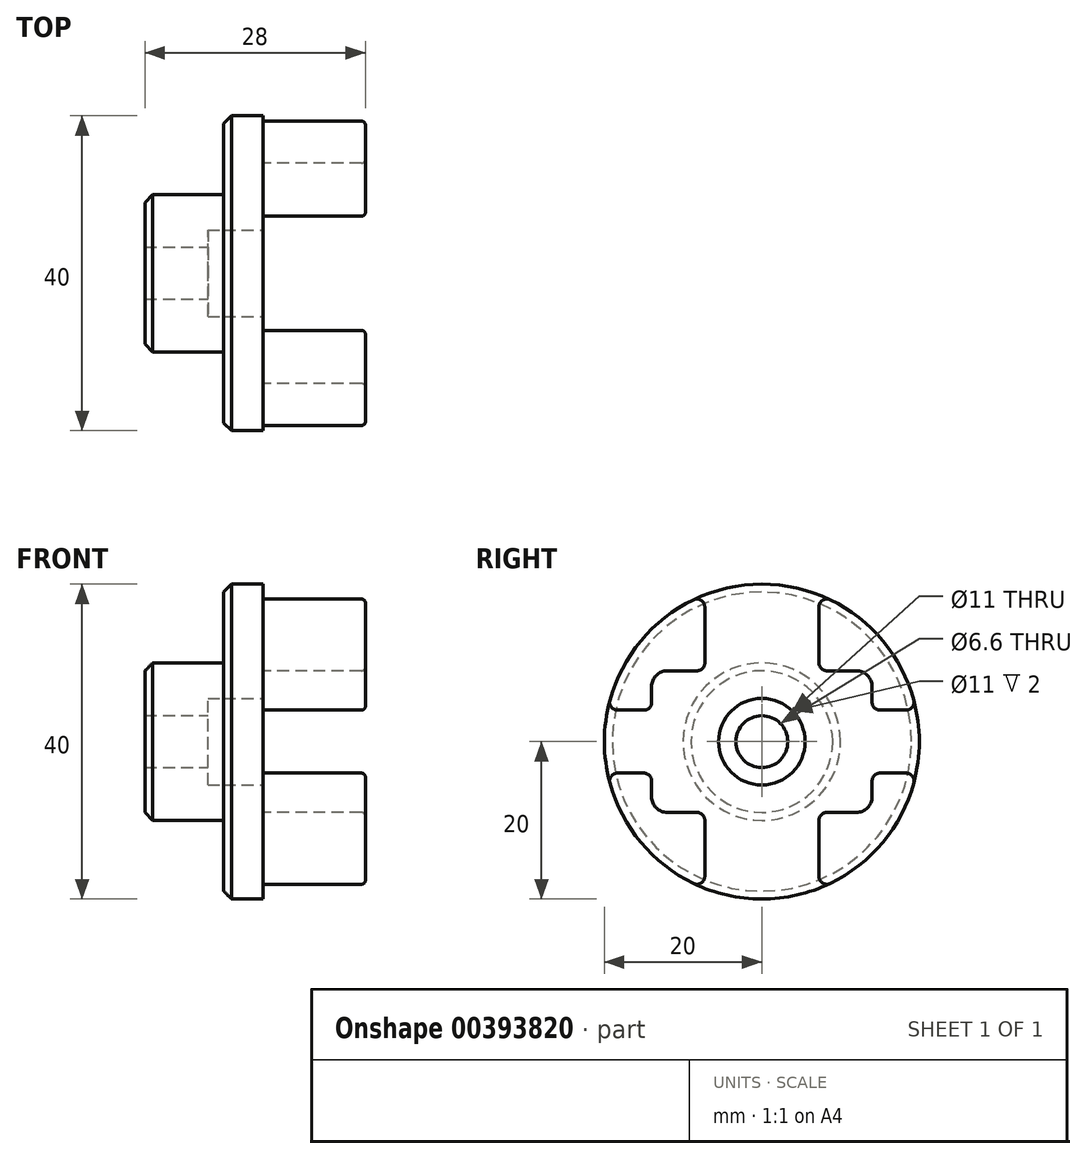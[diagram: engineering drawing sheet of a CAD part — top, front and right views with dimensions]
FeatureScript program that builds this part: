
annotation { "Feature Type Name" : "Feature", "Feature Type Description" : "" }
export const myFeature = defineFeature(function(context is Context, id is Id, definition is map)
    precondition{}
    {
        {
            var Q0;
            Q0=qCreatedBy(makeId("Front.planeOp"),FACE);
            var sketch = newSketch(context, id + "F0", { "sketchPlane" : qUnion([Q0])});
            skLineSegment(sketch, "E0", {"start": v(0, 0) * mm, "end": v(51.78, 0) * mm, "construction": true});
            skLineSegment(sketch, "E1", {"start": v(0, 10) * mm, "end": v(10, 10) * mm});
            skLineSegment(sketch, "E2", {"start": v(10, 10) * mm, "end": v(10, 0) * mm});
            skLineSegment(sketch, "E3", {"start": v(10, 0) * mm, "end": v(0, 0) * mm});
            skLineSegment(sketch, "E4", {"start": v(0, 0) * mm, "end": v(0, 10) * mm});
            skSolve(sketch);
        }
        {
            var Q0;
            Q0=qSketchRegion(id+"F0",true);
            var Q1;
            Q1=sQuery(id+"F0.wireOp",EDGE,"E0");
            revolve(context, id + "F1", {"entities" : qUnion([Q0]), "axis" : qUnion([Q1]), "revolveType" : RevolveType.FULL});
        }
        {
            var Q0;
            Q0=makeQuery(id+"F1.opRevolve","SWEPT_FACE",FACE,{"disambiguationData":[OSD([sQuery(id+"F0.wireOp",EDGE,"E2")])]});
            var sketch = newSketch(context, id + "F2", { "sketchPlane" : qUnion([Q0])});
            skLineSegment(sketch, "E5", {"start": v(-8.25, 5.65) * mm, "end": v(-8.25, -5.65) * mm});
            skLineSegment(sketch, "E6", {"start": v(0, 0) * mm, "end": v(0, 17.13) * mm, "construction": true});
            skLineSegment(sketch, "E7.MirrorCS", {"start": v(8.25, 5.65) * mm, "end": v(8.25, -5.65) * mm});
            skArc(sketch, "E8.0", {"start": v(-8.25, 5.65) * mm, "mid": v(-10, 0) * mm, "end": v(-8.25, -5.65) * mm});
            skArc(sketch, "E9.trimOffspring", {"start": v(8.25, -5.65) * mm, "mid": v(10, 0) * mm, "end": v(8.25, 5.65) * mm});
            skSolve(sketch);
        }
        {
            var Q0;
            Q0=qCreatedBy(makeId("Top.planeOp"),FACE);
            var sketch = newSketch(context, id + "F3", { "sketchPlane" : qUnion([Q0])});
            skCircle(sketch, "E10.cCircle", {"center": v(26, 0) * mm, "radius": 12.7 * mm, "construction": true});
            skLineSegment(sketch, "E10.0", {"start": v(26, 12.7) * mm, "end": v(37, 6.35) * mm});
            skLineSegment(sketch, "E10.1", {"start": v(37, 6.35) * mm, "end": v(37, -6.35) * mm});
            skLineSegment(sketch, "E10.2", {"start": v(37, -6.35) * mm, "end": v(26, -12.7) * mm});
            skLineSegment(sketch, "E10.3", {"start": v(26, -12.7) * mm, "end": v(15, -6.35) * mm});
            skLineSegment(sketch, "E10.4", {"start": v(15, -6.35) * mm, "end": v(15, 6.35) * mm});
            skLineSegment(sketch, "E10.5", {"start": v(15, 6.35) * mm, "end": v(26, 12.7) * mm});
            skLineSegment(sketch, "E11", {"start": v(0, 0) * mm, "end": v(49.29, 0) * mm, "construction": true});
            skLineSegment(sketch, "E12.0", {"start": v(10, -10) * mm, "end": v(10, 10) * mm, "construction": true});
            skLineSegment(sketch, "E13", {"start": v(20, -10) * mm, "end": v(0, -10) * mm});
            skSolve(sketch);
        }
        {
            var Q0;
            Q0=makeQuery(id+"F1.opRevolve","SWEPT_FACE",FACE,{"disambiguationData":[OSD([sQuery(id+"F0.wireOp",EDGE,"E2")])]});
            var sketch = newSketch(context, id + "F4", { "sketchPlane" : qUnion([Q0])});
            skCircle(sketch, "E14", {"center": v(0, 0) * mm, "radius": 20 * mm});
            skSolve(sketch);
        }
        {
            var Q0;
            Q0=qSketchRegion(id+"F4",true);
            extrude(context, id + "F5", {"entities" : qUnion([Q0]), "depth" : 5 * mm});
        }
        {
            var Q0;
            Q0=makeQuery(id+"F5.opExtrude","CAP_FACE",FACE,{"disambiguationData":[OSD([sQuery(id+"F4.wireOp",EDGE,"E14")])],"isStart":false});
            var sketch = newSketch(context, id + "F6", { "sketchPlane" : qUnion([Q0])});
            skLineSegment(sketch, "E15", {"start": v(0, -17) * mm, "end": v(0, 21.67) * mm, "construction": true});
            skLineSegment(sketch, "E16", {"start": v(-7.25, -10) * mm, "end": v(-7.25, -17.12) * mm});
            skLineSegment(sketch, "E17", {"start": v(-14, -7) * mm, "end": v(-14, -5) * mm});
            skArc(sketch, "E18.0", {"start": v(-19.3, -5.26) * mm, "mid": v(-15.37, -12.8) * mm, "end": v(-8.68, -18.02) * mm});
            skArc(sketch, "E19.trimOffspring", {"start": v(9.57, -17.56) * mm, "mid": v(19.9, -1.96) * mm, "end": v(12.8, 15.37) * mm});
            skPoint(sketch, "E20.visualSharp", {"position": v(-7.25, -18.64) * mm});
            skArc(sketch, "E20.filletArc", {"start": v(-8.68, -18.02) * mm, "mid": v(-7.72, -17.96) * mm, "end": v(-7.25, -17.12) * mm});
            skLineSegment(sketch, "E21", {"start": v(-18.33, -4) * mm, "end": v(-15, -4) * mm});
            skLineSegment(sketch, "E22", {"start": v(0, 0) * mm, "end": v(-17.48, 0) * mm, "construction": true});
            skPoint(sketch, "E23.newPointB", {"position": v(-12.8, 15.37) * mm});
            skArc(sketch, "E23.filletArc", {"start": v(-18.33, -4) * mm, "mid": v(-19.13, -4.4) * mm, "end": v(-19.3, -5.26) * mm});
            skPoint(sketch, "E24.visualSharp", {"position": v(-14, -4) * mm});
            skArc(sketch, "E24.filletArc", {"start": v(-14, -5) * mm, "mid": v(-14.3, -4.3) * mm, "end": v(-15, -4) * mm});
            skLineSegment(sketch, "E25", {"start": v(-12, -9) * mm, "end": v(-8.25, -9) * mm});
            skPoint(sketch, "E26.visualSharp", {"position": v(-14, -9) * mm});
            skArc(sketch, "E26.filletArc", {"start": v(-14, -7) * mm, "mid": v(-13.41, -8.41) * mm, "end": v(-12, -9) * mm});
            skPoint(sketch, "E27.visualSharp", {"position": v(-7.25, -9) * mm});
            skArc(sketch, "E27.filletArc", {"start": v(-7.25, -10) * mm, "mid": v(-7.54, -9.3) * mm, "end": v(-8.25, -9) * mm});
            skPoint(sketch, "E28.MirrorP", {"position": v(7.25, -18.64) * mm});
            skArc(sketch, "E29.MirrorCS", {"start": v(14, -5) * mm, "mid": v(14.3, -4.3) * mm, "end": v(15, -4) * mm});
            skArc(sketch, "E30.MirrorCS", {"start": v(8.68, -18.02) * mm, "mid": v(7.72, -17.96) * mm, "end": v(7.25, -17.12) * mm});
            skPoint(sketch, "E31.MirrorP", {"position": v(14, -4) * mm});
            skPoint(sketch, "E32.MirrorP", {"position": v(14, -9) * mm});
            skLineSegment(sketch, "E33.MirrorCS", {"start": v(18.33, -4) * mm, "end": v(15, -4) * mm});
            skArc(sketch, "E34.MirrorCS", {"start": v(7.25, -10) * mm, "mid": v(7.54, -9.3) * mm, "end": v(8.25, -9) * mm});
            skPoint(sketch, "E35.MirrorP", {"position": v(7.25, -9) * mm});
            skArc(sketch, "E36.MirrorCS", {"start": v(14, -7) * mm, "mid": v(13.41, -8.41) * mm, "end": v(12, -9) * mm});
            skLineSegment(sketch, "E37.MirrorCS", {"start": v(12, -9) * mm, "end": v(8.25, -9) * mm});
            skArc(sketch, "E38.MirrorCS", {"start": v(18.33, -4) * mm, "mid": v(19.13, -4.4) * mm, "end": v(19.3, -5.26) * mm});
            skArc(sketch, "E39.MirrorCS", {"start": v(19.3, -5.26) * mm, "mid": v(15.37, -12.8) * mm, "end": v(8.68, -18.02) * mm});
            skLineSegment(sketch, "E40.MirrorCS", {"start": v(14, -7) * mm, "end": v(14, -5) * mm});
            skLineSegment(sketch, "E41.MirrorCS", {"start": v(7.25, -10) * mm, "end": v(7.25, -17.12) * mm});
            skPoint(sketch, "E42.MirrorP", {"position": v(14, 9) * mm});
            skArc(sketch, "E43.MirrorCS", {"start": v(19.3, 5.26) * mm, "mid": v(15.37, 12.8) * mm, "end": v(8.68, 18.02) * mm});
            skPoint(sketch, "E44.MirrorP", {"position": v(-7.25, 18.64) * mm});
            skArc(sketch, "E45.MirrorCS", {"start": v(14, 7) * mm, "mid": v(13.41, 8.41) * mm, "end": v(12, 9) * mm});
            skPoint(sketch, "E46.MirrorP", {"position": v(7.25, 9) * mm});
            skArc(sketch, "E47.MirrorCS", {"start": v(-18.33, 4) * mm, "mid": v(-19.13, 4.4) * mm, "end": v(-19.3, 5.26) * mm});
            skArc(sketch, "E48.MirrorCS", {"start": v(-14, 5) * mm, "mid": v(-14.3, 4.3) * mm, "end": v(-15, 4) * mm});
            skArc(sketch, "E49.MirrorCS", {"start": v(7.25, 10) * mm, "mid": v(7.54, 9.3) * mm, "end": v(8.25, 9) * mm});
            skArc(sketch, "E50.MirrorCS", {"start": v(-7.25, 10) * mm, "mid": v(-7.54, 9.3) * mm, "end": v(-8.25, 9) * mm});
            skArc(sketch, "E51.MirrorCS", {"start": v(-14, 7) * mm, "mid": v(-13.41, 8.41) * mm, "end": v(-12, 9) * mm});
            skLineSegment(sketch, "E52.MirrorCS", {"start": v(-12, 9) * mm, "end": v(-8.25, 9) * mm});
            skPoint(sketch, "E53.MirrorP", {"position": v(-7.25, 9) * mm});
            skPoint(sketch, "E54.MirrorP", {"position": v(14, 4) * mm});
            skArc(sketch, "E55.MirrorCS", {"start": v(18.33, 4) * mm, "mid": v(19.13, 4.4) * mm, "end": v(19.3, 5.26) * mm});
            skLineSegment(sketch, "E56.MirrorCS", {"start": v(14, 7) * mm, "end": v(14, 5) * mm});
            skLineSegment(sketch, "E57.MirrorCS", {"start": v(-7.25, 10) * mm, "end": v(-7.25, 17.12) * mm});
            skLineSegment(sketch, "E58.MirrorCS", {"start": v(-14, 7) * mm, "end": v(-14, 5) * mm});
            skArc(sketch, "E59.MirrorCS", {"start": v(-19.3, 5.26) * mm, "mid": v(-15.37, 12.8) * mm, "end": v(-8.68, 18.02) * mm});
            skPoint(sketch, "E60.MirrorP", {"position": v(-14, 4) * mm});
            skPoint(sketch, "E61.MirrorP", {"position": v(-14, 9) * mm});
            skArc(sketch, "E62.MirrorCS", {"start": v(-8.68, 18.02) * mm, "mid": v(-7.72, 17.96) * mm, "end": v(-7.25, 17.12) * mm});
            skLineSegment(sketch, "E63.MirrorCS", {"start": v(12, 9) * mm, "end": v(8.25, 9) * mm});
            skLineSegment(sketch, "E64.MirrorCS", {"start": v(18.33, 4) * mm, "end": v(15, 4) * mm});
            skLineSegment(sketch, "E65.MirrorCS", {"start": v(7.25, 10) * mm, "end": v(7.25, 17.12) * mm});
            skPoint(sketch, "E66.MirrorP", {"position": v(7.25, 18.64) * mm});
            skArc(sketch, "E67.MirrorCS", {"start": v(14, 5) * mm, "mid": v(14.3, 4.3) * mm, "end": v(15, 4) * mm});
            skArc(sketch, "E68.MirrorCS", {"start": v(8.68, 18.02) * mm, "mid": v(7.72, 17.96) * mm, "end": v(7.25, 17.12) * mm});
            skLineSegment(sketch, "E69.MirrorCS", {"start": v(-18.33, 4) * mm, "end": v(-15, 4) * mm});
            skSolve(sketch);
        }
        {
            var Q0;
            Q0=qSketchRegion(id+"F6",true);
            extrude(context, id + "F7", {"entities" : qUnion([Q0]), "depth" : 13 * mm});
        }
        {
            var Q0;
            Q0=makeQuery(id+"F7.opExtrude","CAP_EDGE",EDGE,{"disambiguationData":[OSD([sQuery(id+"F6.wireOp",EDGE,"E69.MirrorCS")])],"isStart":false});
            var Q1;
            Q1=makeQuery(id+"F7.opExtrude","CAP_EDGE",EDGE,{"disambiguationData":[OSD([sQuery(id+"F6.wireOp",EDGE,"E47.MirrorCS")])],"isStart":false});
            var Q2;
            Q2=makeQuery(id+"F7.opExtrude","CAP_EDGE",EDGE,{"disambiguationData":[OSD([sQuery(id+"F6.wireOp",EDGE,"E59.MirrorCS")])],"isStart":false});
            var Q3;
            Q3=makeQuery(id+"F7.opExtrude","CAP_EDGE",EDGE,{"disambiguationData":[OSD([sQuery(id+"F6.wireOp",EDGE,"E62.MirrorCS")])],"isStart":false});
            var Q4;
            Q4=makeQuery(id+"F7.opExtrude","CAP_EDGE",EDGE,{"disambiguationData":[OSD([sQuery(id+"F6.wireOp",EDGE,"E18.0")])],"isStart":false});
            var Q5;
            Q5=makeQuery(id+"F7.opExtrude","CAP_EDGE",EDGE,{"disambiguationData":[OSD([sQuery(id+"F6.wireOp",EDGE,"E39.MirrorCS")])],"isStart":false});
            var Q6;
            Q6=makeQuery(id+"F7.opExtrude","CAP_EDGE",EDGE,{"disambiguationData":[OSD([sQuery(id+"F6.wireOp",EDGE,"E43.MirrorCS")])],"isStart":false});
            fillet(context, id + "F8", {"entities" : qUnion([Q0, Q1, Q2, Q3, Q4, Q5, Q6]), "radius" : 0.5 * mm, "tangentPropagation" : true, "allowEdgeOverflow" : false});
        }
        {
            var Q0;
            Q0=makeQuery(id+"FUz6FhBA3sICmdU_1.opExtrude","CAP_FACE",FACE,{"disambiguationData":[OSD([sQuery(id+"F3.wireOp",EDGE,"E10.0"),sQuery(id+"F3.wireOp",EDGE,"E10.1"),sQuery(id+"F3.wireOp",EDGE,"E10.2"),sQuery(id+"F3.wireOp",EDGE,"E10.3"),sQuery(id+"F3.wireOp",EDGE,"E10.4"),sQuery(id+"F3.wireOp",EDGE,"E10.5")])],"isStart":false});
            var sketch = newSketch(context, id + "F9", { "sketchPlane" : qUnion([Q0])});
            skCircle(sketch, "E70.0", {"center": v(32, 0) * mm, "radius": 8.08 * mm, "construction": true});
            skCircle(sketch, "E71", {"center": v(32, 0) * mm, "radius": 3.75 * mm});
            skSolve(sketch);
        }
        {
            var Q0;
            Q0=makeQuery(id+"F1.opRevolve","SWEPT_EDGE",EDGE,{"disambiguationData":[OSD([sQuery(id+"F0.wireOp",EDGE,"E1"),sQuery(id+"F0.wireOp",EDGE,"E4")])]});
            var Q1;
            Q1=makeQuery(id+"F5.opExtrude","CAP_EDGE",EDGE,{"disambiguationData":[OSD([sQuery(id+"F4.wireOp",EDGE,"E14")])],"isStart":true});
            chamfer(context, id + "F10", {"entities" : qUnion([Q0, Q1]), "width" : 1 * mm, "tangentPropagation" : true});
        }
        {
            var Q0;
            Q0=makeQuery(id+"F5.opExtrude","CAP_FACE",FACE,{"disambiguationData":[OSD([sQuery(id+"F4.wireOp",EDGE,"E14")])],"isStart":false});
            var sketch = newSketch(context, id + "F11", { "sketchPlane" : qUnion([Q0])});
            skCircle(sketch, "E72.0", {"center": v(0, 0) * mm, "radius": 20 * mm, "construction": true});
            skSolve(sketch);
        }
        {
            var Q0;
            Q0=sQuery(id+"F11.wireOp",VERTEX,"E72.0.center");
            var Q1;
            Q1=makeQuery(id+"F1.opRevolve","SWEPT_BODY",BODY,{"disambiguationData":[OSD([sQuery(id+"F0.wireOp",EDGE,"E1"),sQuery(id+"F0.wireOp",EDGE,"E2"),sQuery(id+"F0.wireOp",EDGE,"E3"),sQuery(id+"F0.wireOp",EDGE,"E4")])]});
            var Q2;
            Q2=makeQuery(id+"F5.opExtrude","SWEPT_BODY",BODY,{"disambiguationData":[OSD([sQuery(id+"F4.wireOp",EDGE,"E14")])]});
            hole(context, id + "F12", {"style" : HoleStyle.C_BORE, "endStyle" : HoleEndStyle.THROUGH, "holeDiameter" : 6.6 * mm, "cBoreDiameter" : 11 * mm, "cBoreDepth" : 7 * mm, "isTappedThrough" : true, "tappedDepth" : 12 * mm, "tapClearance" : 3, "locations" : qUnion([Q0]), "scope" : qUnion([Q1, Q2])});
        }
    });
